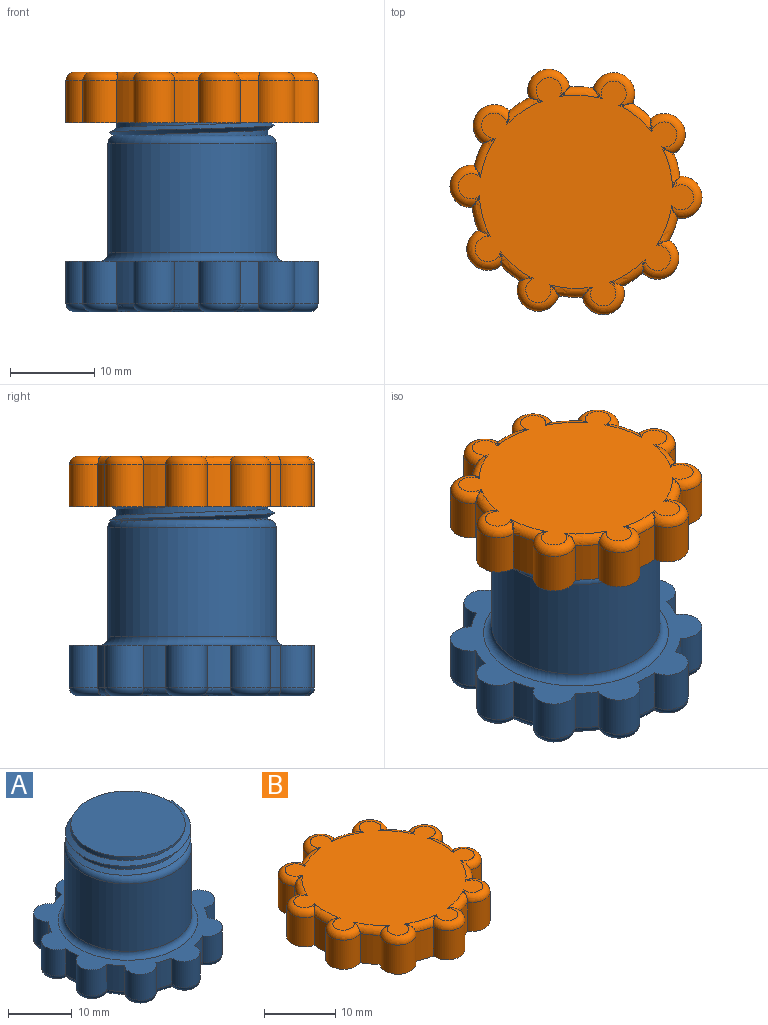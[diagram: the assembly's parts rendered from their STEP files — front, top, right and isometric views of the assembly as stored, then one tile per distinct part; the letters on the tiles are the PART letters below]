
ASSEMBLY  parts=2 mates=1
PART A: 50 faces, bbox 29.2x30.4x24.5 mm
  f0: cylinder r=12.5mm len=5mm, axis (0,0,-1), area 14.2mm2, adj f1,f19,f20,f38
  f1: cylinder r=2.5mm len=5mm, axis (0,0,-1), area 41.8mm2, adj f0,f2,f20,f36
  f2: cylinder r=12.5mm len=5mm, axis (0,0,-1), area 14.2mm2, adj f1,f3,f20,f34
  f3: cylinder r=2.5mm len=5mm, axis (0,0,-1), area 41.8mm2, adj f2,f4,f20,f32
  f4: cylinder r=12.5mm len=5mm, axis (0,0,-1), area 14.2mm2, adj f3,f5,f20,f30
  f5: cylinder r=2.5mm len=5mm, axis (0,0,-1), area 41.8mm2, adj f4,f6,f20,f28
  f6: cylinder r=12.5mm len=5mm, axis (0,0,-1), area 14.2mm2, adj f5,f7,f20,f26
  f7: cylinder r=2.5mm len=5mm, axis (0,0,-1), area 41.8mm2, adj f6,f8,f20,f24
  f8: cylinder r=12.5mm len=5mm, axis (0,0,-1), area 14.2mm2, adj f7,f9,f20,f22
  f9: cylinder r=2.5mm len=5mm, axis (0,0,-1), area 41.8mm2, adj f8,f10,f20,f23
  f10: cylinder r=12.5mm len=5mm, axis (0,0,-1), area 14.2mm2, adj f9,f11,f20,f25
  f11: cylinder r=2.5mm len=5mm, axis (0,0,-1), area 41.8mm2, adj f10,f12,f20,f27
  f12: cylinder r=12.5mm len=5mm, axis (0,0,-1), area 14.2mm2, adj f11,f13,f20,f29
  f13: cylinder r=2.5mm len=5mm, axis (0,0,-1), area 41.8mm2, adj f12,f14,f20,f31
  f14: cylinder r=12.5mm len=5mm, axis (0,0,-1), area 14.2mm2, adj f13,f15,f20,f33
  f15: cylinder r=2.5mm len=5mm, axis (0,0,-1), area 41.8mm2, adj f14,f16,f20,f35
  f16: cylinder r=12.5mm len=5mm, axis (0,0,-1), area 14.2mm2, adj f15,f17,f20,f37
  f17: cylinder r=2.5mm len=5mm, axis (0,0,-1), area 41.8mm2, adj f16,f18,f20,f39
  f18: cylinder r=12.5mm len=5mm, axis (0,0,-1), area 14.2mm2, adj f17,f19,f20,f41
  f19: cylinder r=2.5mm len=5mm, axis (0,0,-1), area 41.8mm2, adj f0,f18,f20,f40
  f20: plane 30x28.78mm, normal (0,0,1), area 213.1mm2, adj f0,f1,f2,f3,f4,f5,f6,f7
  f21: plane 28x26.78mm, normal (0,0,-1), area 478.8mm2, adj f22,f23,f24,f25,f26,f27,f28,f29
  f22: torus R=11.5mm, axis (0,0,1), area 6.4mm2, adj f8,f21,f23,f24
  f23: torus R=1.5mm, axis (0,0,1), area 13.3mm2, adj f9,f21,f22,f25
  f24: torus R=1.5mm, axis (0,0,1), area 13.3mm2, adj f7,f21,f22,f26
  f25: torus R=11.5mm, axis (0,0,1), area 6.4mm2, adj f10,f21,f23,f27
  f26: torus R=11.5mm, axis (0,0,1), area 6.4mm2, adj f6,f21,f24,f28
  f27: torus R=1.5mm, axis (0,0,1), area 13.3mm2, adj f11,f21,f25,f29
  f28: torus R=1.5mm, axis (0,0,1), area 13.3mm2, adj f5,f21,f26,f30
  f29: torus R=11.5mm, axis (0,0,1), area 6.4mm2, adj f12,f21,f27,f31
  f30: torus R=11.5mm, axis (0,0,1), area 6.4mm2, adj f4,f21,f28,f32
  f31: torus R=1.5mm, axis (0,0,1), area 13.3mm2, adj f13,f21,f29,f33
  f32: torus R=1.5mm, axis (0,0,1), area 13.3mm2, adj f3,f21,f30,f34
  f33: torus R=11.5mm, axis (0,0,1), area 6.4mm2, adj f14,f21,f31,f35
  f34: torus R=11.5mm, axis (0,0,1), area 6.4mm2, adj f2,f21,f32,f36
  f35: torus R=1.5mm, axis (0,0,1), area 13.3mm2, adj f15,f21,f33,f37
  f36: torus R=1.5mm, axis (0,0,1), area 13.3mm2, adj f1,f21,f34,f38
  f37: torus R=11.5mm, axis (0,0,1), area 6.4mm2, adj f16,f21,f35,f39
  f38: torus R=11.5mm, axis (0,0,1), area 6.4mm2, adj f0,f21,f36,f40
  f39: torus R=1.5mm, axis (0,0,1), area 13.3mm2, adj f17,f21,f37,f41
  f40: torus R=1.5mm, axis (0,0,1), area 13.3mm2, adj f19,f21,f38,f41
  f41: torus R=11.5mm, axis (0,0,1), area 6.4mm2, adj f18,f21,f39,f40
  f42: cylinder r=10mm len=20mm, axis (0,0,-1), area 816.8mm2, adj f48,f49
  f43: cylinder r=9mm len=18mm, axis (0,0,-1), area 100.7mm2, adj f44,f45,f46,f47,f49
  f44: plane 18x18mm, normal (0,0,1), area 254.5mm2, adj f43
  f45: plane 1x0.87mm, normal (0,1,0), area 0.4mm2, adj f43,f46,f47
  f46: bspline ~22.78x19.73mm, area 101.8mm2, adj f43,f45,f47,f49
  f47: bspline ~22.78x19.73mm, area 114.9mm2, adj f43,f45,f46,f49
  f48: torus R=11mm, axis (0,0,1), area 102.3mm2, adj f20,f42
  f49: torus R=9mm, axis (0,0,1), area 81mm2, adj f42,f43,f46,f47
PART B: 49 faces, bbox 29.5x30.7x6.7 mm
  f0: plane 30.33x29.11mm, normal (0,0,-1), area 316.6mm2, adj f1,f2,f3,f4,f5,f6,f7,f8
  f1: cylinder r=12.5mm len=5mm, axis (0,0,-1), area 14.2mm2, adj f0,f2,f20,f40
  f2: cylinder r=2.5mm len=5mm, axis (0,0,-1), area 41.8mm2, adj f0,f1,f3,f38
  f3: cylinder r=12.5mm len=5mm, axis (0,0,-1), area 14.2mm2, adj f0,f2,f4,f36
  f4: cylinder r=2.5mm len=5mm, axis (0,0,-1), area 41.8mm2, adj f0,f3,f5,f34
  f5: cylinder r=12.5mm len=5mm, axis (0,0,-1), area 14.2mm2, adj f0,f4,f6,f32
  f6: cylinder r=2.5mm len=5mm, axis (0,0,-1), area 41.8mm2, adj f0,f5,f7,f30
  f7: cylinder r=12.5mm len=5mm, axis (0,0,-1), area 14.2mm2, adj f0,f6,f8,f28
  f8: cylinder r=2.5mm len=5mm, axis (0,0,-1), area 41.8mm2, adj f0,f7,f9,f26
  f9: cylinder r=12.5mm len=5mm, axis (0,0,-1), area 14.2mm2, adj f0,f8,f10,f24
  f10: cylinder r=2.5mm len=5mm, axis (0,0,-1), area 41.8mm2, adj f0,f9,f11,f25
  f11: cylinder r=12.5mm len=5mm, axis (0,0,-1), area 14.2mm2, adj f0,f10,f12,f27
  f12: cylinder r=2.5mm len=5mm, axis (0,0,-1), area 41.8mm2, adj f0,f11,f13,f29
  f13: cylinder r=12.5mm len=5mm, axis (0,0,-1), area 14.2mm2, adj f0,f12,f14,f31
  f14: cylinder r=2.5mm len=5mm, axis (0,0,-1), area 41.8mm2, adj f0,f13,f15,f33
  f15: cylinder r=12.5mm len=5mm, axis (0,0,-1), area 14.2mm2, adj f0,f14,f16,f35
  f16: cylinder r=2.5mm len=5mm, axis (0,0,-1), area 41.8mm2, adj f0,f15,f17,f37
  f17: cylinder r=12.5mm len=5mm, axis (0,0,-1), area 14.2mm2, adj f0,f16,f18,f39
  f18: cylinder r=2.5mm len=5mm, axis (0,0,-1), area 41.8mm2, adj f0,f17,f19,f41
  f19: cylinder r=12.5mm len=5mm, axis (0,0,-1), area 14.2mm2, adj f0,f18,f20,f43
  f20: cylinder r=2.5mm len=5mm, axis (0,0,-1), area 41.8mm2, adj f0,f1,f19,f42
  f21: plane 28x26.78mm, normal (0,0,1), area 478.8mm2, adj f24,f25,f26,f27,f28,f29,f30,f31
  f22: cylinder r=9.3mm len=18.6mm, axis (0,0,1), area 93.1mm2, adj f0,f23,f44,f45,f46,f48
  f23: plane 18.6x18.6mm, normal (0,0,-1), area 271.7mm2, adj f22,f47
  f24: torus R=11.5mm, axis (0,0,1), area 6.4mm2, adj f9,f21,f25,f26
  f25: torus R=1.5mm, axis (0,0,1), area 13.3mm2, adj f10,f21,f24,f27
  f26: torus R=1.5mm, axis (0,0,1), area 13.3mm2, adj f8,f21,f24,f28
  f27: torus R=11.5mm, axis (0,0,1), area 6.4mm2, adj f11,f21,f25,f29
  f28: torus R=11.5mm, axis (0,0,1), area 6.4mm2, adj f7,f21,f26,f30
  f29: torus R=1.5mm, axis (0,0,1), area 13.3mm2, adj f12,f21,f27,f31
  f30: torus R=1.5mm, axis (0,0,1), area 13.3mm2, adj f6,f21,f28,f32
  f31: torus R=11.5mm, axis (0,0,1), area 6.4mm2, adj f13,f21,f29,f33
  f32: torus R=11.5mm, axis (0,0,1), area 6.4mm2, adj f5,f21,f30,f34
  f33: torus R=1.5mm, axis (0,0,1), area 13.3mm2, adj f14,f21,f31,f35
  f34: torus R=1.5mm, axis (0,0,1), area 13.3mm2, adj f4,f21,f32,f36
  f35: torus R=11.5mm, axis (0,0,1), area 6.4mm2, adj f15,f21,f33,f37
  f36: torus R=11.5mm, axis (0,0,1), area 6.4mm2, adj f3,f21,f34,f38
  f37: torus R=1.5mm, axis (0,0,1), area 13.3mm2, adj f16,f21,f35,f39
  f38: torus R=1.5mm, axis (0,0,1), area 13.3mm2, adj f2,f21,f36,f40
  f39: torus R=11.5mm, axis (0,0,1), area 6.4mm2, adj f17,f21,f37,f41
  f40: torus R=11.5mm, axis (0,0,1), area 6.4mm2, adj f1,f21,f38,f42
  f41: torus R=1.5mm, axis (0,0,1), area 13.3mm2, adj f18,f21,f39,f43
  f42: torus R=1.5mm, axis (0,0,1), area 13.3mm2, adj f20,f21,f40,f43
  f43: torus R=11.5mm, axis (0,0,1), area 6.4mm2, adj f19,f21,f41,f42
  f44: plane 0.65x0.38mm, normal (0,1,0), area 0.1mm2, adj f0,f22,f48
  f45: bspline ~22.98x19.9mm, area 85.1mm2, adj f0,f22,f46,f48
  f46: plane 0.75x0.65mm, normal (0,-1,0), area 0.2mm2, adj f22,f45,f47,f48
  f47: cylinder r=9.3mm len=9.3mm, axis (0,0,1), area 2.7mm2, adj f23,f46,f48
  f48: bspline ~22.98x19.9mm, area 90.7mm2, adj f22,f44,f45,f46,f47
PLACE A rot(axis=(0,0,1),15deg) t=(-3.88,-0.16,10.96)mm
PLACE B rot(axis=(0,0,1),15deg) t=(-3.88,-0.16,11.94)mm
MATE slider A.f43 <-> B.f22  axis (0,0,1) through (-3.88,-0.16,32.46)mm
